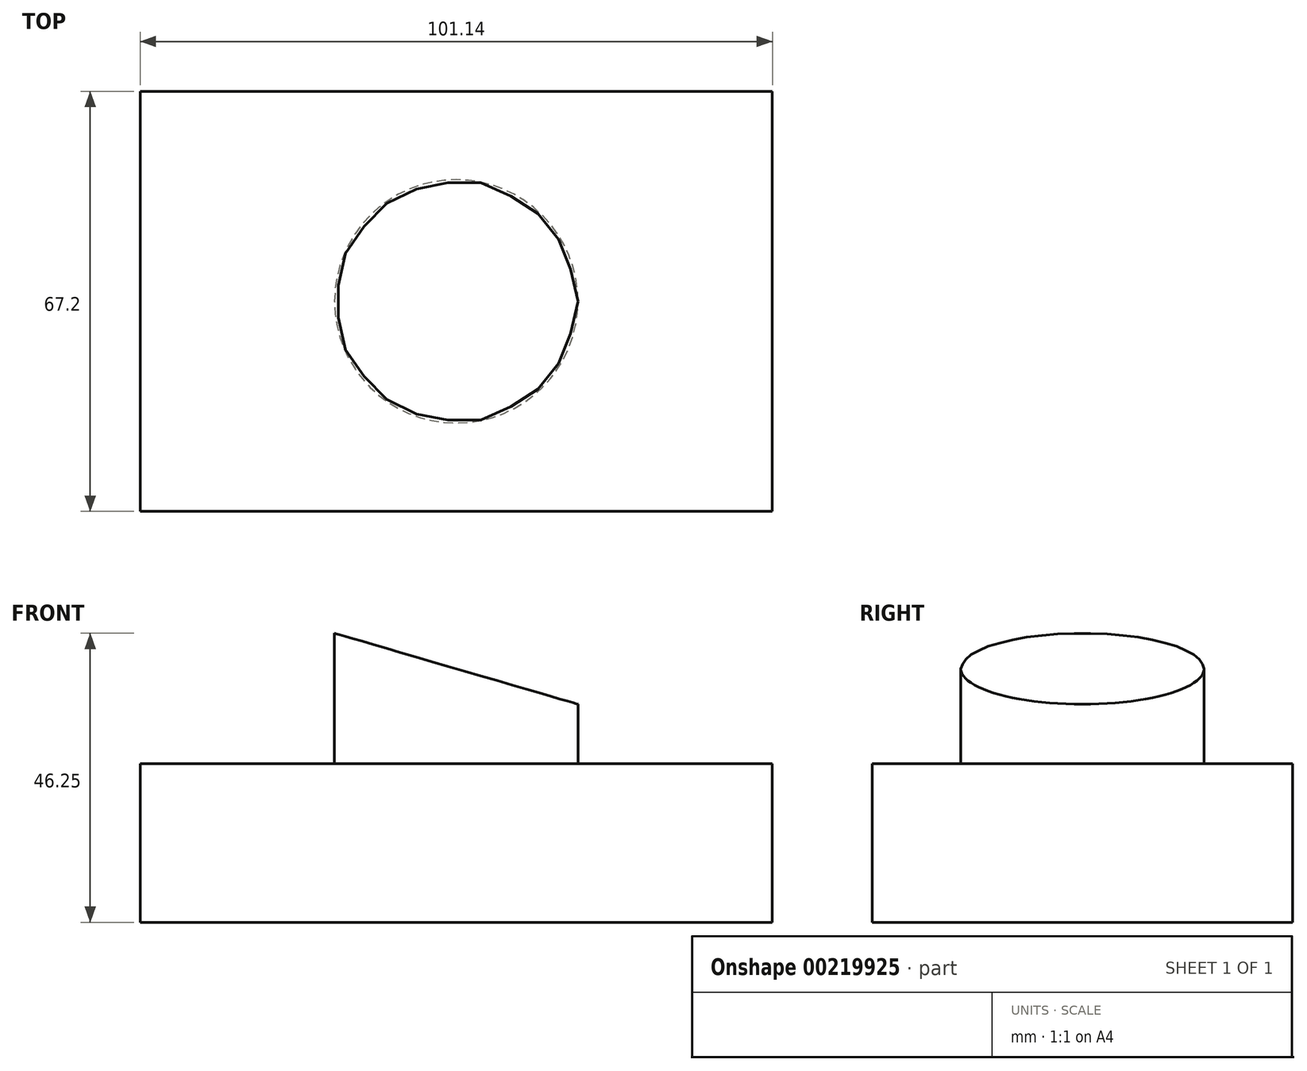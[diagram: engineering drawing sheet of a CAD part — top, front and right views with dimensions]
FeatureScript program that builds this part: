
annotation { "Feature Type Name" : "Feature", "Feature Type Description" : "" }
export const myFeature = defineFeature(function(context is Context, id is Id, definition is map)
    precondition{}
    {
        {
            var Q0;
            Q0=qCreatedBy(makeId("Top.planeOp"),FACE);
            var sketch = newSketch(context, id + "F0", { "sketchPlane" : qUnion([Q0])});
            skLineSegment(sketch, "E0.bottom", {"start": v(50.57, -33.6) * mm, "end": v(-50.57, -33.6) * mm});
            skLineSegment(sketch, "E0.top", {"start": v(50.57, 33.6) * mm, "end": v(-50.57, 33.6) * mm});
            skLineSegment(sketch, "E0.left", {"start": v(50.57, -33.6) * mm, "end": v(50.57, 33.6) * mm});
            skLineSegment(sketch, "E0.right", {"start": v(-50.57, -33.6) * mm, "end": v(-50.57, 33.6) * mm});
            skPoint(sketch, "E0.middle", {"position": v(0, 0) * mm});
            skSolve(sketch);
        }
        {
            var Q0;
            Q0 = qSketchRegion(id + "F0", true);
            extrude(context, id + "F1", {"entities" : qUnion([Q0]), "depth" : 25.4 * mm});
        }
        {
            var Q0;
            Q0=makeQuery(id+"F1.opExtrude","CAP_FACE",FACE,{"disambiguationData":[OSD([sQuery(id+"F0.wireOp",EDGE,"E0.bottom"),sQuery(id+"F0.wireOp",EDGE,"E0.top"),sQuery(id+"F0.wireOp",EDGE,"E0.left"),sQuery(id+"F0.wireOp",EDGE,"E0.right")])],"isStart":false});
            var sketch = newSketch(context, id + "F2", { "sketchPlane" : qUnion([Q0])});
            skCircle(sketch, "E1", {"center": v(0, 0) * mm, "radius": 19.47 * mm});
            skSolve(sketch);
        }
        {
            var Q0;
            Q0 = qSketchRegion(id + "F2", true);
            extrude(context, id + "F3", {"entities" : qUnion([Q0]), "operationType" : NewBodyOperationType.ADD, "depth" : 25.4 * mm});
        }
        {
            var Q0;
            Q0=makeQuery(id+"F1.opExtrude","SWEPT_FACE",FACE,{"disambiguationData":[OSD([sQuery(id+"F0.wireOp",EDGE,"E0.bottom")])]});
            var sketch = newSketch(context, id + "F4", { "sketchPlane" : qUnion([Q0])});
            skLineSegment(sketch, "E2", {"start": v(20.55, 34.58) * mm, "end": v(-19.63, 46.3) * mm});
            skLineSegment(sketch, "E3", {"start": v(-19.63, 46.3) * mm, "end": v(-19.63, 51.6) * mm});
            skLineSegment(sketch, "E4", {"start": v(-19.63, 51.6) * mm, "end": v(20.55, 51.6) * mm});
            skLineSegment(sketch, "E5", {"start": v(20.55, 51.6) * mm, "end": v(20.55, 34.58) * mm});
            skSolve(sketch);
        }
        {
            var Q0;
            Q0 = qSketchRegion(id + "F4", true);
            extrude(context, id + "F5", {"entities" : qUnion([Q0]), "operationType" : NewBodyOperationType.REMOVE, "oppositeDirection" : true, "depth" : 82.8 * mm});
        }
    });
